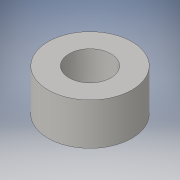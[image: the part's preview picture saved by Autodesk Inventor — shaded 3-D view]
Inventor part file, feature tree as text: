
AUTODESK INVENTOR PART (.ipt)
format: ipt  version: 2016 (Build 200138000, 138)  size: 90,112 bytes
history: native  units: in
note: dims shown in document units (in); Inventor stores cm internally (conversion verified against a paired STEP export)
features: extrude x1, sketch x1
ambient origin geometry x8: Origin, YZ Plane, XZ Plane, XY Plane, X Axis, Y Axis, Z Axis, Center Point
bodies: Solid1 (feature_tree)
feature tree (2):
  extrude  "Extrusion1"  Depth=0.5in
  sketch  "Sketch1"  dims[d0=0.5in d2=1.0in d3=0.5in d4=0.0in]
